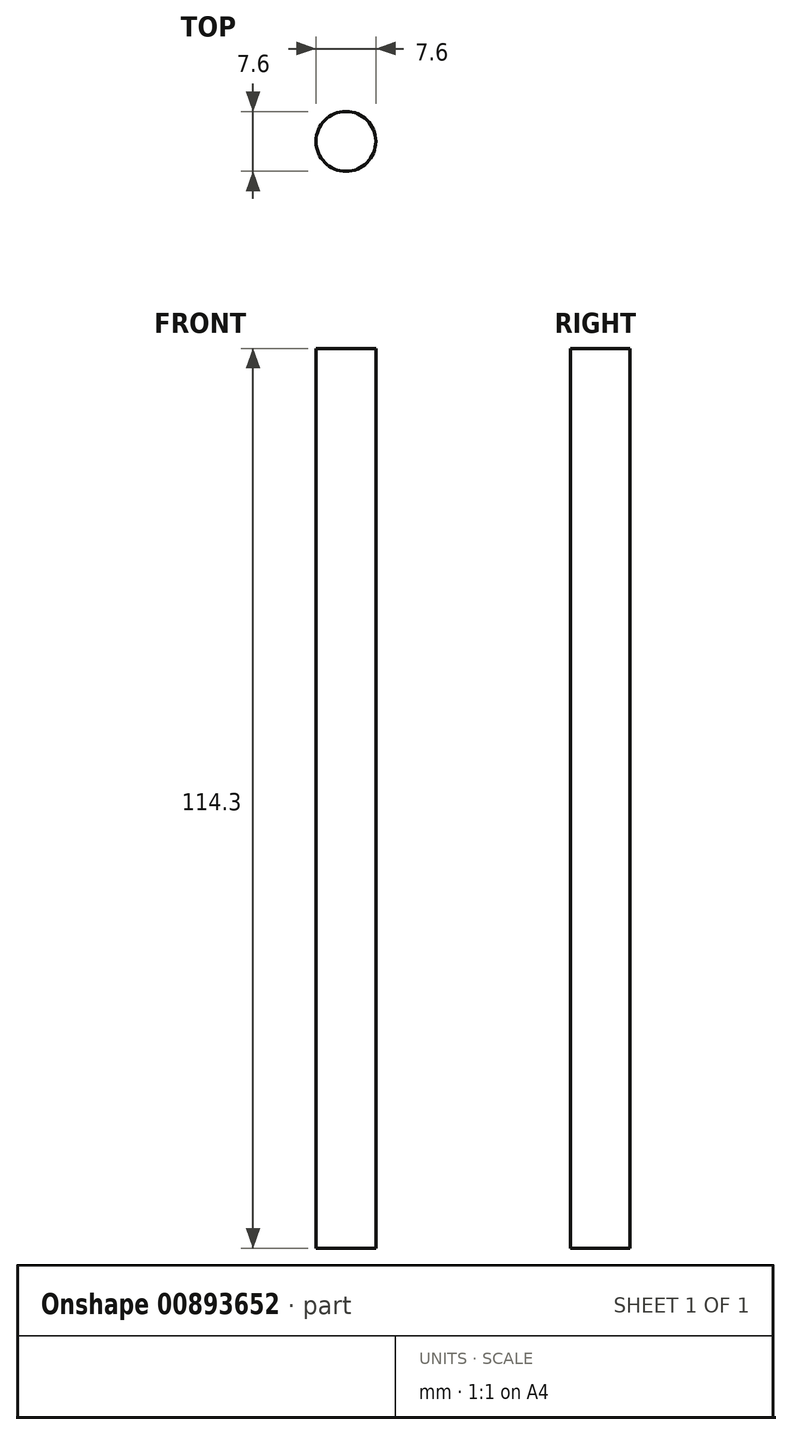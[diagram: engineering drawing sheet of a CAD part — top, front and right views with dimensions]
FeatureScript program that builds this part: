
annotation { "Feature Type Name" : "Feature", "Feature Type Description" : "" }
export const myFeature = defineFeature(function(context is Context, id is Id, definition is map)
    precondition{}
    {
        {
            var Q0;
            Q0=qCreatedBy(makeId("Top.planeOp"),FACE);
            var sketch = newSketch(context, id + "F0", { "sketchPlane" : qUnion([Q0])});
            skCircle(sketch, "E0", {"center": v(0, 0) * mm, "radius": 3.8 * mm});
            skSolve(sketch);
        }
        {
            var Q0;
            Q0 = qSketchRegion(id + "F0", true);
            extrude(context, id + "F1", {"entities" : qUnion([Q0]), "depth" : 114.3 * mm, "offsetDistance" : 25.4 * mm});
        }
    });
